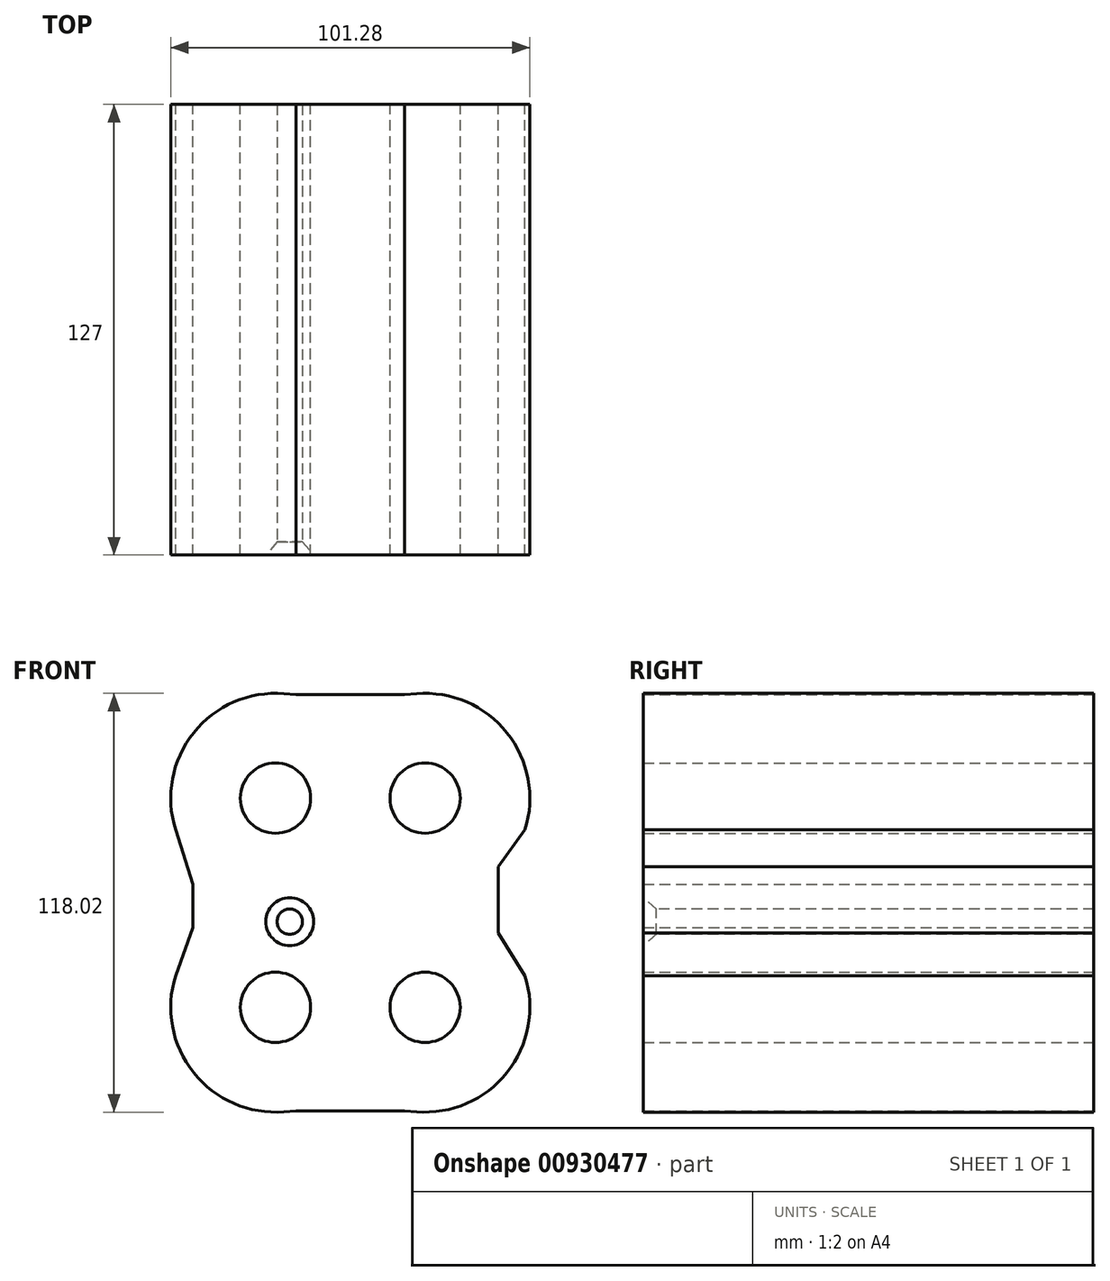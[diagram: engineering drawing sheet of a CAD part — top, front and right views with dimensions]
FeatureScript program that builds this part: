
annotation { "Feature Type Name" : "Feature", "Feature Type Description" : "" }
export const myFeature = defineFeature(function(context is Context, id is Id, definition is map)
    precondition{}
    {
        {
            var Q0;
            Q0=qCreatedBy(makeId("Front.planeOp"),FACE);
            var sketch = newSketch(context, id + "F0", { "sketchPlane" : qUnion([Q0])});
            skLineSegment(sketch, "E0", {"start": v(-60.94, 0) * mm, "end": v(57.56, 0) * mm, "construction": true});
            skArc(sketch, "E1", {"start": v(-49.26, 20.58) * mm, "mid": v(-44.2, 47.89) * mm, "end": v(-18.7, 58.91) * mm});
            skLineSegment(sketch, "E2", {"start": v(0, 0) * mm, "end": v(0, 53.25) * mm, "construction": true});
            skArc(sketch, "E3.MirrorCS", {"start": v(49.26, 20.58) * mm, "mid": v(44.2, 47.89) * mm, "end": v(18.7, 58.91) * mm});
            skLineSegment(sketch, "E4.MirrorCS", {"start": v(60.94, 0) * mm, "end": v(-57.56, 0) * mm, "construction": true});
            skArc(sketch, "E5.MirrorCS", {"start": v(49.26, -20.58) * mm, "mid": v(44.2, -47.89) * mm, "end": v(18.7, -58.91) * mm});
            skArc(sketch, "E6.MirrorCS", {"start": v(-49.26, -20.58) * mm, "mid": v(-44.2, -47.89) * mm, "end": v(-18.7, -58.91) * mm});
            skCircle(sketch, "E7", {"center": v(-21.1, 29.47) * mm, "radius": 9.91 * mm});
            skCircle(sketch, "E8.MirrorC", {"center": v(21.1, 29.47) * mm, "radius": 9.91 * mm});
            skCircle(sketch, "E9.MirrorC", {"center": v(-21.1, -29.47) * mm, "radius": 9.91 * mm});
            skCircle(sketch, "E10.MirrorC", {"center": v(21.1, -29.47) * mm, "radius": 9.91 * mm});
            skLineSegment(sketch, "E11", {"start": v(-18.7, 58.91) * mm, "end": v(-15.3, 58.64) * mm});
            skLineSegment(sketch, "E12", {"start": v(-15.3, 58.64) * mm, "end": v(0, 58.64) * mm});
            skLineSegment(sketch, "E13.MirrorCS", {"start": v(15.3, 58.64) * mm, "end": v(0, 58.64) * mm});
            skLineSegment(sketch, "E14.MirrorCS", {"start": v(18.7, 58.91) * mm, "end": v(15.3, 58.64) * mm});
            skLineSegment(sketch, "E15.MirrorCS", {"start": v(-18.7, -58.91) * mm, "end": v(-15.3, -58.64) * mm});
            skLineSegment(sketch, "E16.MirrorCS", {"start": v(-15.3, -58.64) * mm, "end": v(0, -58.64) * mm});
            skLineSegment(sketch, "E17.MirrorCS", {"start": v(15.3, -58.64) * mm, "end": v(0, -58.64) * mm});
            skLineSegment(sketch, "E18.MirrorCS", {"start": v(18.7, -58.91) * mm, "end": v(15.3, -58.64) * mm});
            skLineSegment(sketch, "E19", {"start": v(-49.26, 20.58) * mm, "end": v(-44.42, 5.24) * mm});
            skLineSegment(sketch, "E20", {"start": v(-44.42, 5.24) * mm, "end": v(-44.42, -7.02) * mm});
            skLineSegment(sketch, "E21", {"start": v(-44.42, -7.02) * mm, "end": v(-49.26, -20.58) * mm});
            skLineSegment(sketch, "E22", {"start": v(49.26, 20.58) * mm, "end": v(41.76, 10.17) * mm});
            skLineSegment(sketch, "E23", {"start": v(41.76, 10.17) * mm, "end": v(41.76, -8.45) * mm});
            skLineSegment(sketch, "E24", {"start": v(41.76, -8.45) * mm, "end": v(49.26, -20.58) * mm});
            skSolve(sketch);
        }
        {
            var Q0;
            Q0 = qSketchRegion(id + "F0", true);
            extrude(context, id + "F1", {"entities" : qUnion([Q0]), "endBound" : BoundingType.SYMMETRIC, "depth" : 127 * mm, "offsetDistance" : 25.4 * mm});
        }
        {
            var Q0;
            Q0=makeQuery(id+"F1.opExtrude","CAP_FACE",FACE,{"disambiguationData":[OSD([sQuery(id+"F0.wireOp",EDGE,"E1"),sQuery(id+"F0.wireOp",EDGE,"E3.MirrorCS"),sQuery(id+"F0.wireOp",EDGE,"E5.MirrorCS"),sQuery(id+"F0.wireOp",EDGE,"E6.MirrorCS"),sQuery(id+"F0.wireOp",EDGE,"E7"),sQuery(id+"F0.wireOp",EDGE,"E8.MirrorC"),sQuery(id+"F0.wireOp",EDGE,"E9.MirrorC"),sQuery(id+"F0.wireOp",EDGE,"E10.MirrorC"),sQuery(id+"F0.wireOp",EDGE,"E11"),sQuery(id+"F0.wireOp",EDGE,"E12"),sQuery(id+"F0.wireOp",EDGE,"E13.MirrorCS"),sQuery(id+"F0.wireOp",EDGE,"E14.MirrorCS"),sQuery(id+"F0.wireOp",EDGE,"E15.MirrorCS"),sQuery(id+"F0.wireOp",EDGE,"E16.MirrorCS"),sQuery(id+"F0.wireOp",EDGE,"E17.MirrorCS"),sQuery(id+"F0.wireOp",EDGE,"E18.MirrorCS"),sQuery(id+"F0.wireOp",EDGE,"E19"),sQuery(id+"F0.wireOp",EDGE,"E20"),sQuery(id+"F0.wireOp",EDGE,"E21"),sQuery(id+"F0.wireOp",EDGE,"E22"),sQuery(id+"F0.wireOp",EDGE,"E23"),sQuery(id+"F0.wireOp",EDGE,"E24")])],"isStart":false});
            var sketch = newSketch(context, id + "F2", { "sketchPlane" : qUnion([Q0])});
            skPoint(sketch, "E25", {"position": v(-17.07, -5.33) * mm});
            skSolve(sketch);
        }
        {
            var Q0;
            Q0=sQuery(id+"F2.wireOp",VERTEX,"E25");
            var Q1;
            Q1=makeQuery(id+"F1.opExtrude","SWEPT_BODY",BODY,{"disambiguationData":[OSD([sQuery(id+"F0.wireOp",EDGE,"E1"),sQuery(id+"F0.wireOp",EDGE,"E3.MirrorCS"),sQuery(id+"F0.wireOp",EDGE,"E5.MirrorCS"),sQuery(id+"F0.wireOp",EDGE,"E6.MirrorCS"),sQuery(id+"F0.wireOp",EDGE,"E7"),sQuery(id+"F0.wireOp",EDGE,"E8.MirrorC"),sQuery(id+"F0.wireOp",EDGE,"E9.MirrorC"),sQuery(id+"F0.wireOp",EDGE,"E10.MirrorC"),sQuery(id+"F0.wireOp",EDGE,"E11"),sQuery(id+"F0.wireOp",EDGE,"E12"),sQuery(id+"F0.wireOp",EDGE,"E13.MirrorCS"),sQuery(id+"F0.wireOp",EDGE,"E14.MirrorCS"),sQuery(id+"F0.wireOp",EDGE,"E15.MirrorCS"),sQuery(id+"F0.wireOp",EDGE,"E16.MirrorCS"),sQuery(id+"F0.wireOp",EDGE,"E17.MirrorCS"),sQuery(id+"F0.wireOp",EDGE,"E18.MirrorCS"),sQuery(id+"F0.wireOp",EDGE,"E19"),sQuery(id+"F0.wireOp",EDGE,"E20"),sQuery(id+"F0.wireOp",EDGE,"E21"),sQuery(id+"F0.wireOp",EDGE,"E22"),sQuery(id+"F0.wireOp",EDGE,"E23"),sQuery(id+"F0.wireOp",EDGE,"E24")])]});
            hole(context, id + "F3", {"style" : HoleStyle.C_SINK, "endStyle" : HoleEndStyle.THROUGH, "standardTappedOrClearance" : lookupTablePath({ "fit" : "Normal (ASME)", "standard" : "ANSI", "size" : "1/4", "type" : "Clearance" }), "standardBlindInLast" : lookupTablePath({ "fit" : "Normal", "standard" : "ANSI", "engagement" : "75%", "pitch" : "20 tpi", "size" : "1/4", "type" : "Clearance & tapped" }), "holeDiameter" : 7.14 * mm, "cSinkDiameter" : 13.5 * mm, "cSinkAngle" : 82 * degree, "majorDiameter" : 6.35 * mm, "isTappedThrough" : true, "tappedDepth" : 12.7 * mm, "tapClearance" : 3, "startFromSketch" : true, "locations" : qUnion([Q0]), "scope" : qUnion([Q1])});
        }
    });
